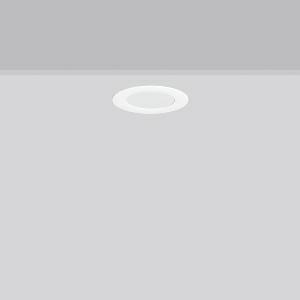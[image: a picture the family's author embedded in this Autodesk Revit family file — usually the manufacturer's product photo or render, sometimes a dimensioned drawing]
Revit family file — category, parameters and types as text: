
# Revit family: toledo_flat_round_e_901451_002_1_bd59
name_source: partatom
category: Lighting Fixtures
units: mm (PartAtom-declared; Revit-internal decimal feet)

## family parameters
Cut with Voids When Loaded = No
Host = Face
Light Source = No
Part Type = Normal
Room Calculation Point = No
Round Connector Dimension = Use Diameter
Shared = No

## types (1)
- TOLEDO FLAT round E (1 x LED Modul 840, 530 lm, 4000)
    Apparent Load = 5 VA
    CIE Flux Codes = 48 79 96 100 100
    Color Rendering = 80
    Color Temperature = 4000
    Default Elevation = 1800 mm
    Description = Series: TOLEDO FLAT round
Ultra thin recessed downlight. Housing: die-cast aluminium. Light guide and diffuser made of non-yellowing PMMA, opal matt. Ceiling installation with spring system. Mounting depth depends on ceiling strength. Including separate LED converter with connecting cable 250 mm. Suitable for through-wiring with separately available accessories. Surface mounted housing as accessory for all sizes. Retrofittable decorative cylinders made of chintz fabric as accessory, optional with satin finish plastic diffuser. Through-wiring box (5 pole) available as accessory. 
Colour: white
Diameter: 148 mm
Height: 2 mm
Cut-out diameter: 128 mm
Recess height: 27-53 mm
Luminaire: recess height: 31-51 mm
Lamp: LED
Socket: without socket
Colour temperature: 4000K
Colour rendering index (CRI): 80
System power: 5 W
Rated luminous flux: 530 lm
Luminous efficiency: 106 lm/W
Control gear: Regulated power supply
Protection class: II
Type of protection: IP 54
    Height = 0 mm  [stored 0 ft]
    Lamp = 1 x LED Modul 840
    Lamp Light Flux = 530 lm
    Lamp count = 1
    Length = 148 mm
    Lifetime = 50000 h
    Luminous efficacy = 106 lm/W
    Manufacturer = RZB
    ModVariant = No
    Model = 901451.002.1
    Mounting Place = Ceiling
    Mounting Type = Recessed
    Number of Poles = 1
    OnlyDefault = Yes
    Power Factor = 1
    Product Name = TOLEDO FLAT round E
    Product group = Recessed downlights
    ProductGroupID = 402
    Protection Class = Protection class II
    Protection Degree = IP 20
    RLX_Detail_Level = 1
    RLX_Emergency_Light_Flux = 0 lm
    RLX_Emergency_Type = 0
    RLX_Emergency_Type_DB = No
    RlxData = <blob elided: 75109 chars, md5=f4478a8c>
    Socket = socket
    Standby Power = 0 W
    System Light Flux = 530 lm
    System Power = 5 W
    Type Comments = Product without accessories
    Type Image = 901451.002.jpg
    URL = http://relux.com
    VarID = ---
    Voltage = 230 V
    Voltage Range = 220-240 V
    Weight = 0.00 kg
    Width = 0 mm  [stored 0 ft]

note: [stored X ft] marks values corroborated as IEEE doubles in the binary element streams (Revit-internal decimal feet)

## geometry (parser evidence)
native form markers: Blend x4, Sweep x10
no freeform markers — native parametric forms only
